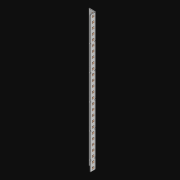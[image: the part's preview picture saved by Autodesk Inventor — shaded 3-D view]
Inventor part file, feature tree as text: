
AUTODESK INVENTOR PART (.ipt)
format: ipt  version: 2021 (Build 250183000, 183)  size: 1,280,512 bytes
history: native  units: in
note: dims shown in document units (in); Inventor stores cm internally (conversion verified against a paired STEP export)
features: extrude x56, other x54, sketch x4, pattern_linear x2, sheet_metal_op x1
ambient origin geometry x8: Origin, YZ Plane, XZ Plane, XY Plane, X Axis, Y Axis, Z Axis, Center Point
bodies: Solid1 (feature_tree)
feature tree (117):
  pattern_linear  "Rectangular Pattern1"  Spacing1=0.5in  [1 undecoded]
  pattern_linear  "Rectangular Pattern3"  Count1=27  [1 undecoded]
  extrude  "Extrusion1"  Depth=0.5in
  extrude  "Extrusion2"  Depth=0.5in
  sketch  "Sketch1"  dims[d0=0.182in]
  other  "Srf1"
  sketch  "Sketch3"  dims[d1=0.063in d2=0.0in]
  other  "Srf3"
  other  "Srf4"
  other  "Srf5"
  other  "Srf6"
  other  "Srf7"
  other  "Srf8"
  other  "Srf9"
  other  "Srf10"
  other  "Srf11"
  other  "Srf12"
  other  "Srf13"
  other  "Srf14"
  other  "Srf15"
  other  "Srf16"
  other  "Srf17"
  other  "Srf18"
  other  "Srf19"
  other  "Srf20"
  other  "Srf21"
  other  "Srf22"
  other  "Srf23"
  other  "Srf24"
  other  "Srf25"
  other  "Srf26"
  other  "Srf27"
  other  "Srf28"
  other  "Srf29"
  other  "Srf142"
  other  "Srf143"
  other  "Srf144"
  other  "Srf145"
  other  "Srf146"
  other  "Srf147"
  other  "Srf148"
  other  "Srf149"
  other  "Srf150"
  other  "Srf151"
  other  "Srf152"
  other  "Srf153"
  other  "Srf154"
  other  "Srf155"
  other  "Srf156"
  other  "Srf157"
  other  "Srf158"
  other  "Srf159"
  other  "Srf160"
  other  "Srf161"
  other  "Srf162"
  other  "Srf163"
  other  "Srf164"
  other  "Srf165"
  other  "Srf166"
  other  "Srf167"
  sketch  "Sketch4"  dims[d6=0.182in]
  sketch  "Sketch5"  dims[d7=0.063in d8=0.0in d11=0.5in d12=0.3937in d14=0.5in d18=10.6299in d20=0.5in d21=4.0in d22=0.0in d23=0.841in d24=0.0in]
  sheet_metal_op  "Fold1"
  extrude  "ExtrusionSrf1"  TaperAngle=0.0deg  [1 undecoded]
  extrude  "ExtrusionSrf3"  Depth=0.5in TaperAngle=0.0deg
  extrude  "ExtrusionSrf4"  [1 undecoded]
  extrude  "ExtrusionSrf5"  [1 undecoded]
  extrude  "ExtrusionSrf6"  [1 undecoded]
  extrude  "ExtrusionSrf7"  [1 undecoded]
  extrude  "ExtrusionSrf8"  [1 undecoded]
  extrude  "ExtrusionSrf9"  [1 undecoded]
  extrude  "ExtrusionSrf10"  [1 undecoded]
  extrude  "ExtrusionSrf11"  [1 undecoded]
  extrude  "ExtrusionSrf12"  [1 undecoded]
  extrude  "ExtrusionSrf13"  [1 undecoded]
  extrude  "ExtrusionSrf14"  [1 undecoded]
  extrude  "ExtrusionSrf15"  [1 undecoded]
  extrude  "ExtrusionSrf16"  [1 undecoded]
  extrude  "ExtrusionSrf17"  [1 undecoded]
  extrude  "ExtrusionSrf18"  [1 undecoded]
  extrude  "ExtrusionSrf19"  [1 undecoded]
  extrude  "ExtrusionSrf20"  [1 undecoded]
  extrude  "ExtrusionSrf21"  [1 undecoded]
  extrude  "ExtrusionSrf22"  [1 undecoded]
  extrude  "ExtrusionSrf23"  [1 undecoded]
  extrude  "ExtrusionSrf24"  [1 undecoded]
  extrude  "ExtrusionSrf25"  [1 undecoded]
  extrude  "ExtrusionSrf26"  [1 undecoded]
  extrude  "ExtrusionSrf27"  [1 undecoded]
  extrude  "ExtrusionSrf28"  [1 undecoded]
  extrude  "ExtrusionSrf29"  [1 undecoded]
  extrude  "ExtrusionSrf142"  [1 undecoded]
  extrude  "ExtrusionSrf143"  [1 undecoded]
  extrude  "ExtrusionSrf144"  [1 undecoded]
  extrude  "ExtrusionSrf145"  [1 undecoded]
  extrude  "ExtrusionSrf146"  [1 undecoded]
  extrude  "ExtrusionSrf147"  [1 undecoded]
  extrude  "ExtrusionSrf148"  [1 undecoded]
  extrude  "ExtrusionSrf149"  [1 undecoded]
  extrude  "ExtrusionSrf150"  [1 undecoded]
  extrude  "ExtrusionSrf151"  [1 undecoded]
  extrude  "ExtrusionSrf152"  [1 undecoded]
  extrude  "ExtrusionSrf153"  [1 undecoded]
  extrude  "ExtrusionSrf154"  [1 undecoded]
  extrude  "ExtrusionSrf155"  [1 undecoded]
  extrude  "ExtrusionSrf156"  [1 undecoded]
  extrude  "ExtrusionSrf157"  [1 undecoded]
  extrude  "ExtrusionSrf158"  [1 undecoded]
  extrude  "ExtrusionSrf159"  [1 undecoded]
  extrude  "ExtrusionSrf160"  [1 undecoded]
  extrude  "ExtrusionSrf161"  [1 undecoded]
  extrude  "ExtrusionSrf162"  [1 undecoded]
  extrude  "ExtrusionSrf163"  [1 undecoded]
  extrude  "ExtrusionSrf164"  [1 undecoded]
  extrude  "ExtrusionSrf165"  [1 undecoded]
  extrude  "ExtrusionSrf166"  [1 undecoded]
  extrude  "ExtrusionSrf167"  [1 undecoded]
note: 55 required parameter values undecoded (feature->parameter linkage not recoverable at this tier; creation-order binding heuristic only, values carry confidence <= 0.55)
